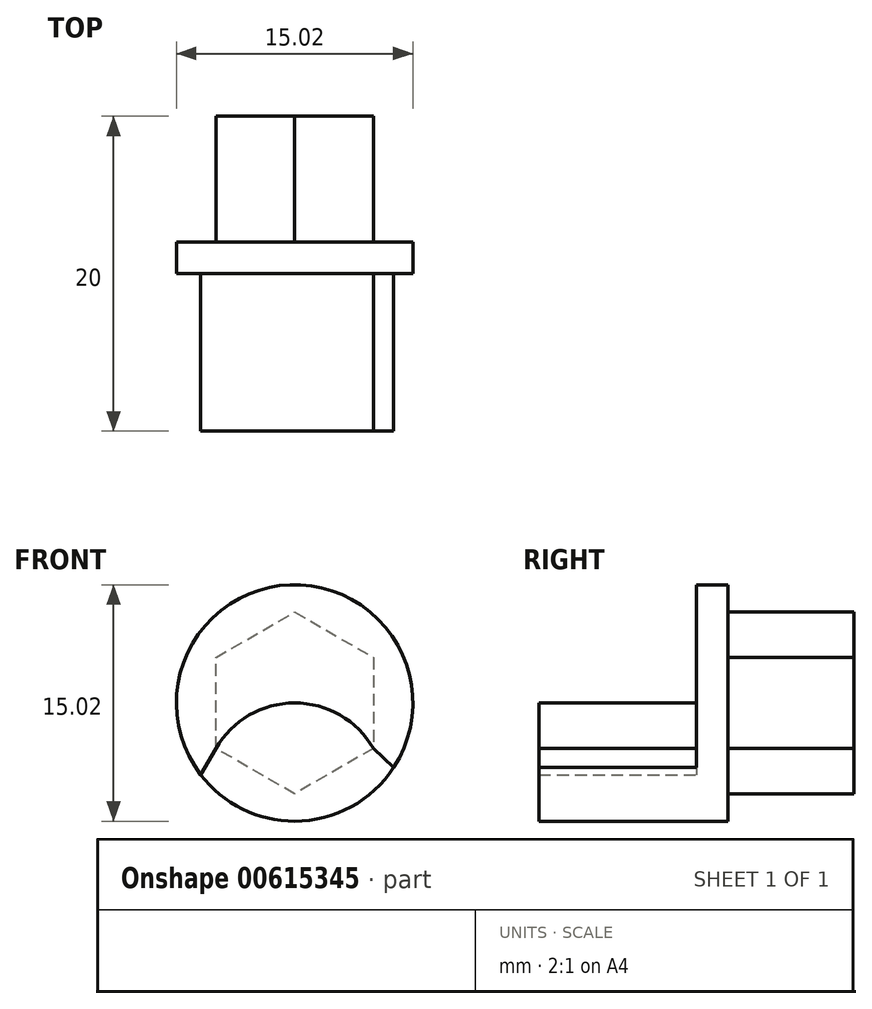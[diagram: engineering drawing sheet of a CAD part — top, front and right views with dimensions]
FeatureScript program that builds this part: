
annotation { "Feature Type Name" : "Feature", "Feature Type Description" : "" }
export const myFeature = defineFeature(function(context is Context, id is Id, definition is map)
    precondition{}
    {
        {
            var Q0;
            Q0=qCreatedBy(makeId("Front.planeOp"),FACE);
            var sketch = newSketch(context, id + "F0", { "sketchPlane" : qUnion([Q0])});
            skCircle(sketch, "E0.cCircle", {"center": v(0, 0) * mm, "radius": 5 * mm, "construction": true});
            skLineSegment(sketch, "E0.0", {"start": v(0, 5.77) * mm, "end": v(5, 2.89) * mm});
            skLineSegment(sketch, "E0.1", {"start": v(5, 2.89) * mm, "end": v(5, -2.89) * mm});
            skLineSegment(sketch, "E0.2", {"start": v(5, -2.89) * mm, "end": v(0, -5.77) * mm});
            skLineSegment(sketch, "E0.3", {"start": v(0, -5.77) * mm, "end": v(-5, -2.89) * mm});
            skLineSegment(sketch, "E0.4", {"start": v(-5, -2.89) * mm, "end": v(-5, 2.89) * mm});
            skLineSegment(sketch, "E0.5", {"start": v(-5, 2.89) * mm, "end": v(0, 5.77) * mm});
            skPoint(sketch, "E0.0.midPoint", {"position": v(2.5, 4.33) * mm});
            skLineSegment(sketch, "E1", {"start": v(0, 5.77) * mm, "end": v(0, -5.77) * mm, "construction": true});
            skSolve(sketch);
        }
        {
            var Q0;
            Q0=makeQuery(id+"F0.imprint","IMPRINT",FACE,{"disambiguationData":[TD([[makeQuery(id+"F0.imprint","IMPRINT",EDGE,{"derivedFrom":sQuery(id+"F0.wireOp",EDGE,"E0.0")}),-1.0]])]});
            extrude(context, id + "F1", {"entities" : qUnion([Q0]), "depth" : 10 * mm, "offsetDistance" : 25.4 * mm});
        }
        {
            var Q0;
            Q0=makeQuery(id+"F1.opExtrude","CAP_FACE",FACE,{"disambiguationData":[OSD([sQuery(id+"F0.wireOp",EDGE,"E0.0"),sQuery(id+"F0.wireOp",EDGE,"E0.1"),sQuery(id+"F0.wireOp",EDGE,"E0.2"),sQuery(id+"F0.wireOp",EDGE,"E0.3"),sQuery(id+"F0.wireOp",EDGE,"E0.4"),sQuery(id+"F0.wireOp",EDGE,"E0.5")])],"isStart":false});
            var sketch = newSketch(context, id + "F2", { "sketchPlane" : qUnion([Q0])});
            skCircle(sketch, "E2", {"center": v(0, -5.77) * mm, "radius": 5.77 * mm});
            skSolve(sketch);
        }
        {
            var Q0;
            {var subQ1=makeQuery(id+"F1.opExtrude","CAP_EDGE",EDGE,{"disambiguationData":[OSD([sQuery(id+"F0.wireOp",EDGE,"E0.2")])],"isStart":false});Q0=makeQuery(id+"F2.imprint","IMPRINT",FACE,{"disambiguationData":[TD([[makeQuery(id+"F2.imprint","IMPRINT",EDGE,{"derivedFrom":subQ1}),-1.0]])]});}
            extrude(context, id + "F3", {"entities" : qUnion([Q0]), "operationType" : NewBodyOperationType.ADD, "depth" : 10 * mm, "offsetDistance" : 25.4 * mm});
        }
        {
            var Q0;
            Q0=makeQuery(id+"F1.opExtrude","CAP_FACE",FACE,{"disambiguationData":[OSD([sQuery(id+"F0.wireOp",EDGE,"E0.0"),sQuery(id+"F0.wireOp",EDGE,"E0.1"),sQuery(id+"F0.wireOp",EDGE,"E0.2"),sQuery(id+"F0.wireOp",EDGE,"E0.3"),sQuery(id+"F0.wireOp",EDGE,"E0.4"),sQuery(id+"F0.wireOp",EDGE,"E0.5")])],"isStart":false});
            var sketch = newSketch(context, id + "F4", { "sketchPlane" : qUnion([Q0])});
            skCircle(sketch, "E3", {"center": v(0, 0) * mm, "radius": 7.5 * mm});
            skSolve(sketch);
        }
        {
            var Q0;
            Q0=makeQuery(id+"F4.imprint","IMPRINT",FACE,{"disambiguationData":[TD([[makeQuery(id+"F4.imprint","IMPRINT",EDGE,{"derivedFrom":sQuery(id+"F4.wireOp",EDGE,"E3")}),1.0]])]});
            extrude(context, id + "F5", {"entities" : qUnion([Q0]), "operationType" : NewBodyOperationType.ADD, "oppositeDirection" : true, "depth" : 2 * mm, "offsetDistance" : 25.4 * mm});
        }
        {
            var Q0;
            {var subQ0=sQuery(id+"F0.wireOp",EDGE,"E0.5");var subQ1=sQuery(id+"F0.wireOp",EDGE,"E0.4");var subQ2=sQuery(id+"F0.wireOp",EDGE,"E0.1");var subQ3=sQuery(id+"F0.wireOp",EDGE,"E0.0");Q0=makeQuery(id+"F5.boolean.opBoolean","MERGE",FACE,{"derivedFrom":[makeQuery(id+"F1.opExtrude","CAP_FACE",FACE,{"disambiguationData":[OSD([subQ3,subQ2,sQuery(id+"F0.wireOp",EDGE,"E0.2"),sQuery(id+"F0.wireOp",EDGE,"E0.3"),subQ1,subQ0])],"isStart":false}),makeQuery(id+"F5.opExtrude","CAP_FACE",FACE,{"disambiguationData":[OSD([subQ3,subQ2,subQ1,subQ0,sQuery(id+"F2.wireOp",EDGE,"E2"),sQuery(id+"F4.wireOp",EDGE,"E3")])],"isStart":true})]});}
            var sketch = newSketch(context, id + "F6", { "sketchPlane" : qUnion([Q0])});
            skLineSegment(sketch, "E4", {"start": v(-5, -2.89) * mm, "end": v(-5.97, -4.56) * mm});
            skLineSegment(sketch, "E5", {"start": v(5, -2.89) * mm, "end": v(6.3, -4.1) * mm});
            skCircle(sketch, "E6.0.0", {"center": v(0, 0) * mm, "radius": 7.5 * mm});
            skSolve(sketch);
        }
        {
            var Q0;
            {var subQ1=sQuery(id+"F6.wireOp",EDGE,"E4");Q0=makeQuery(id+"F6.imprint","IMPRINT",FACE,{"disambiguationData":[TD([[makeQuery(id+"F6.imprint","IMPRINT",EDGE,{"derivedFrom":subQ1}),1.0]])]});}
            var Q1;
            Q1=makeQuery(id+"F3.opExtrude","CAP_FACE",FACE,{"disambiguationData":[OSD([sQuery(id+"F0.wireOp",EDGE,"E0.2"),sQuery(id+"F0.wireOp",EDGE,"E0.3"),sQuery(id+"F2.wireOp",EDGE,"E2")])],"isStart":false});
            extrude(context, id + "F7", {"entities" : qUnion([Q0]), "operationType" : NewBodyOperationType.ADD, "endBound" : BoundingType.UP_TO_SURFACE, "depth" : 25.4 * mm, "endBoundEntityFace" : qUnion([Q1]), "offsetDistance" : 25.4 * mm});
        }
    });
